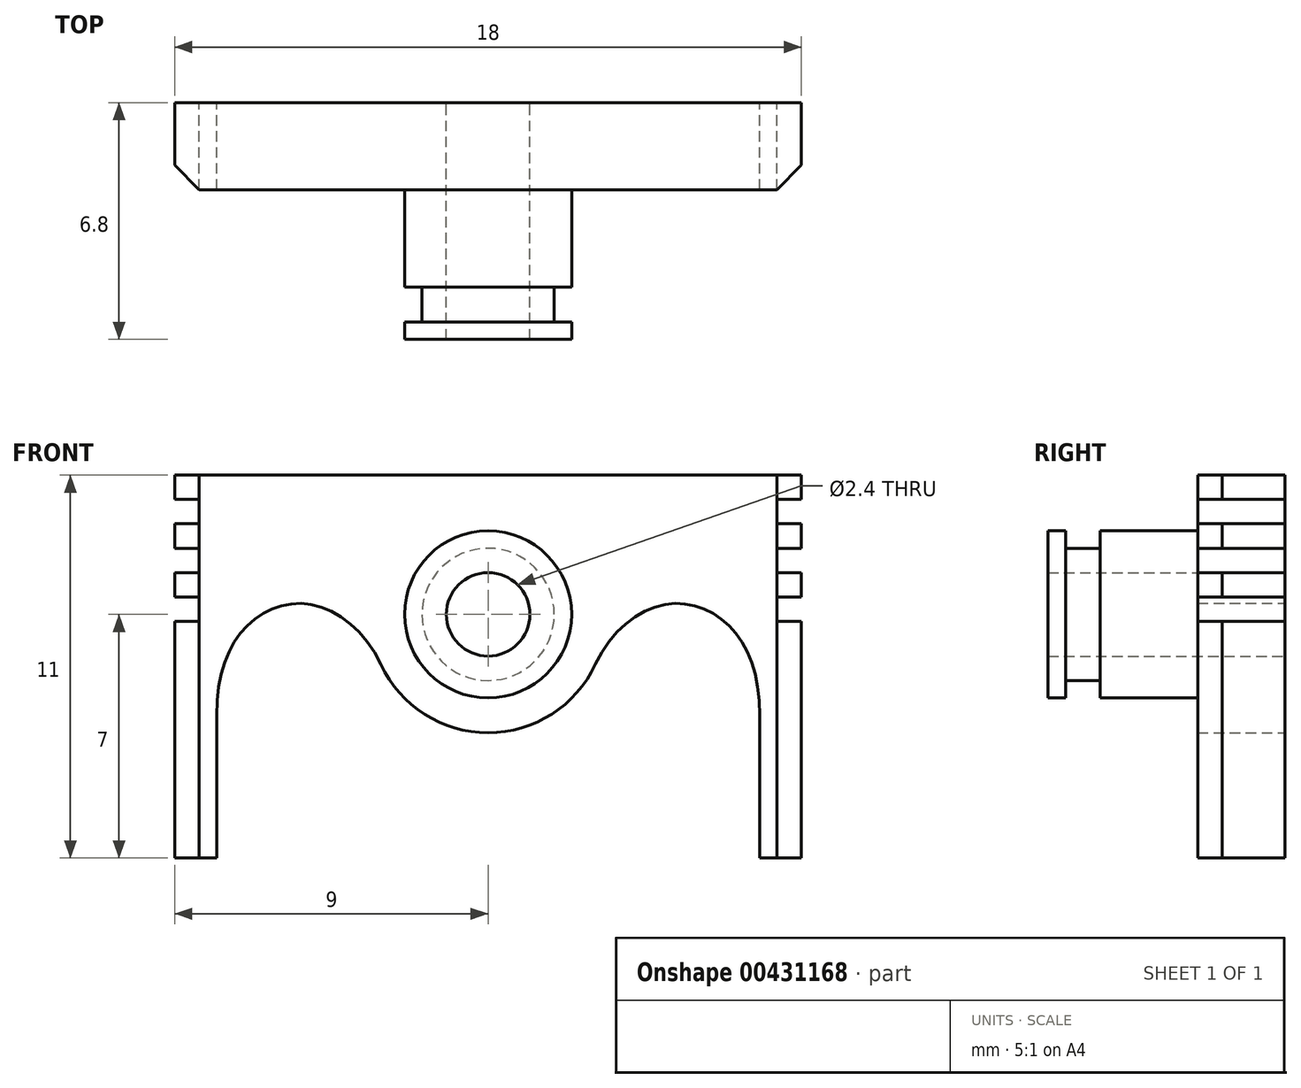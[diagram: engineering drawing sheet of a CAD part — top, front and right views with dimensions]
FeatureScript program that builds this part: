
annotation { "Feature Type Name" : "Feature", "Feature Type Description" : "" }
export const myFeature = defineFeature(function(context is Context, id is Id, definition is map)
    precondition{}
    {
        {
            var Q0;
            Q0=qCreatedBy(makeId("Front.planeOp"),FACE);
            var sketch = newSketch(context, id + "F0", { "sketchPlane" : qUnion([Q0])});
            skLineSegment(sketch, "E0", {"start": v(0, -3.4) * mm, "end": v(0, 25.06) * mm, "construction": true});
            skLineSegment(sketch, "E1.bottom", {"start": v(-9, 4) * mm, "end": v(0, 4) * mm});
            skLineSegment(sketch, "E1.left", {"start": v(-9, 4) * mm, "end": v(-9, 3.3) * mm});
            skArc(sketch, "E2", {"start": v(0, 2.4) * mm, "mid": v(-2.4, 0) * mm, "end": v(0, -2.4) * mm});
            skLineSegment(sketch, "E3.bottom", {"start": v(-9, 3.3) * mm, "end": v(-8.3, 3.3) * mm});
            skLineSegment(sketch, "E3.top", {"start": v(-9, 2.6) * mm, "end": v(-8.3, 2.6) * mm});
            skLineSegment(sketch, "E3.right", {"start": v(-8.3, 3.3) * mm, "end": v(-8.3, 2.6) * mm});
            skLineSegment(sketch, "E4.bottom", {"start": v(-9, 1.9) * mm, "end": v(-8.3, 1.9) * mm});
            skLineSegment(sketch, "E4.top", {"start": v(-9, 1.2) * mm, "end": v(-8.3, 1.2) * mm});
            skLineSegment(sketch, "E4.right", {"start": v(-8.3, 1.9) * mm, "end": v(-8.3, 1.2) * mm});
            skLineSegment(sketch, "E5", {"start": v(-9, 1.9) * mm, "end": v(-9, 2.6) * mm});
            skLineSegment(sketch, "E6", {"start": v(-9, -7) * mm, "end": v(-9, -0.2) * mm});
            skLineSegment(sketch, "E7", {"start": v(-9, -7) * mm, "end": v(-7.8, -7) * mm});
            skLineSegment(sketch, "E8", {"start": v(-7.8, -7) * mm, "end": v(-7.8, -2.9) * mm});
            skLineSegment(sketch, "E9", {"start": v(0, 4) * mm, "end": v(0, 2.4) * mm});
            skLineSegment(sketch, "E10", {"start": v(0, -2.4) * mm, "end": v(0, -3.4) * mm});
            skArc(sketch, "E11", {"start": v(-3.08, -1.44) * mm, "mid": v(-1.83, -2.87) * mm, "end": v(0, -3.4) * mm});
            skFitSpline(sketch, "E12", {"points": [v(-7.8, -2.9) * mm, v(-6.88, -0.29) * mm, v(-5.1, 0.29) * mm, v(-3.08, -1.44) * mm], "startDerivative": vector(0, 10.2) * mm, "endDerivative": vector(3.83, -8.2) * mm});
            skLineSegment(sketch, "E13", {"start": v(-3.08, -1.44) * mm, "end": v(-4.16, 0.88) * mm, "construction": true});
            skLineSegment(sketch, "E14", {"start": v(-9, 0.5) * mm, "end": v(-8.3, 0.5) * mm});
            skLineSegment(sketch, "E15", {"start": v(-8.3, 0.5) * mm, "end": v(-8.3, -0.2) * mm});
            skLineSegment(sketch, "E16", {"start": v(-8.3, -0.2) * mm, "end": v(-9, -0.2) * mm});
            skLineSegment(sketch, "E17.trimOffspring", {"start": v(-9, 0.5) * mm, "end": v(-9, 1.2) * mm});
            skSolve(sketch);
        }
        {
            var Q0;
            Q0=makeQuery(id+"F0.imprint","IMPRINT",FACE,{"disambiguationData":[TD([[makeQuery(id+"F0.imprint","IMPRINT",EDGE,{"derivedFrom":sQuery(id+"F0.wireOp",EDGE,"E1.bottom")}),-1.0]])]});
            extrude(context, id + "F1", {"entities" : qUnion([Q0]), "depth" : 2.5 * mm});
        }
        {
            var Q0;
            Q0=makeQuery(id+"F1.opExtrude","SWEPT_BODY",BODY,{"disambiguationData":[OSD([sQuery(id+"F0.wireOp",EDGE,"E1.bottom"),sQuery(id+"F0.wireOp",EDGE,"E1.left"),sQuery(id+"F0.wireOp",EDGE,"E2"),sQuery(id+"F0.wireOp",EDGE,"E3.bottom"),sQuery(id+"F0.wireOp",EDGE,"E3.top"),sQuery(id+"F0.wireOp",EDGE,"E3.right"),sQuery(id+"F0.wireOp",EDGE,"E4.bottom"),sQuery(id+"F0.wireOp",EDGE,"E4.top"),sQuery(id+"F0.wireOp",EDGE,"E4.right"),sQuery(id+"F0.wireOp",EDGE,"E5"),sQuery(id+"F0.wireOp",EDGE,"E6"),sQuery(id+"F0.wireOp",EDGE,"E7"),sQuery(id+"F0.wireOp",EDGE,"E8"),sQuery(id+"F0.wireOp",EDGE,"E9"),sQuery(id+"F0.wireOp",EDGE,"E10"),sQuery(id+"F0.wireOp",EDGE,"E11"),sQuery(id+"F0.wireOp",EDGE,"E12"),sQuery(id+"F0.wireOp",EDGE,"E14"),sQuery(id+"F0.wireOp",EDGE,"E15"),sQuery(id+"F0.wireOp",EDGE,"E16"),sQuery(id+"F0.wireOp",EDGE,"E17.trimOffspring")])]});
            var Q1;
            Q1=qCreatedBy(makeId("Right.planeOp"),FACE);
            mirror(context, id + "F2", {"operationType" : NewBodyOperationType.ADD, "entities" : qUnion([Q0]), "mirrorPlane" : qUnion([Q1])});
        }
        {
            var Q0;
            Q0=qCreatedBy(makeId("Right.planeOp"),FACE);
            var sketch = newSketch(context, id + "F3", { "sketchPlane" : qUnion([Q0])});
            skLineSegment(sketch, "E18", {"start": v(0, 0) * mm, "end": v(-7.95, 0) * mm, "construction": true});
            skLineSegment(sketch, "E19", {"start": v(-2.5, 2.4) * mm, "end": v(-2.5, 1.2) * mm});
            skLineSegment(sketch, "E20", {"start": v(-2.5, 1.2) * mm, "end": v(-6.8, 1.2) * mm});
            skLineSegment(sketch, "E21", {"start": v(-5.3, 2.4) * mm, "end": v(-2.5, 2.4) * mm});
            skLineSegment(sketch, "E22", {"start": v(-5.3, 2.4) * mm, "end": v(-5.3, 1.9) * mm});
            skLineSegment(sketch, "E23", {"start": v(-5.3, 1.9) * mm, "end": v(-6.3, 1.9) * mm});
            skLineSegment(sketch, "E24", {"start": v(-6.3, 1.9) * mm, "end": v(-6.3, 2.4) * mm});
            skLineSegment(sketch, "E25", {"start": v(-6.3, 2.4) * mm, "end": v(-6.8, 2.4) * mm});
            skLineSegment(sketch, "E26", {"start": v(-6.8, 2.4) * mm, "end": v(-6.8, 1.2) * mm});
            skLineSegment(sketch, "E27", {"start": v(-2.5, 1.2) * mm, "end": v(0, 1.2) * mm});
            skLineSegment(sketch, "E28", {"start": v(0, 1.2) * mm, "end": v(0, 2.4) * mm});
            skLineSegment(sketch, "E29", {"start": v(0, 2.4) * mm, "end": v(-2.5, 2.4) * mm});
            skSolve(sketch);
        }
        {
            var Q0;
            Q0=makeQuery(id+"F1.opExtrude","CAP_EDGE",EDGE,{"disambiguationData":[OSD([sQuery(id+"F0.wireOp",EDGE,"E6")])],"isStart":false});
            var Q1;
            Q1=makeQuery(id+"F2.opPattern","COPY",EDGE,{"derivedFrom":makeQuery(id+"F1.opExtrude","CAP_EDGE",EDGE,{"disambiguationData":[OSD([sQuery(id+"F0.wireOp",EDGE,"E6")])],"isStart":false}),"instanceName":"1"});
            var Q2;
            Q2=makeQuery(id+"F1.opExtrude","CAP_EDGE",EDGE,{"disambiguationData":[OSD([sQuery(id+"F0.wireOp",EDGE,"E1.left")])],"isStart":false});
            var Q3;
            Q3=makeQuery(id+"F1.opExtrude","CAP_EDGE",EDGE,{"disambiguationData":[OSD([sQuery(id+"F0.wireOp",EDGE,"E5")])],"isStart":false});
            var Q4;
            Q4=makeQuery(id+"F1.opExtrude","CAP_EDGE",EDGE,{"disambiguationData":[OSD([sQuery(id+"F0.wireOp",EDGE,"E17.trimOffspring")])],"isStart":false});
            var Q5;
            Q5=makeQuery(id+"F2.opPattern","COPY",EDGE,{"derivedFrom":makeQuery(id+"F1.opExtrude","CAP_EDGE",EDGE,{"disambiguationData":[OSD([sQuery(id+"F0.wireOp",EDGE,"E1.left")])],"isStart":false}),"instanceName":"1"});
            var Q6;
            Q6=makeQuery(id+"F2.opPattern","COPY",EDGE,{"derivedFrom":makeQuery(id+"F1.opExtrude","CAP_EDGE",EDGE,{"disambiguationData":[OSD([sQuery(id+"F0.wireOp",EDGE,"E5")])],"isStart":false}),"instanceName":"1"});
            var Q7;
            Q7=makeQuery(id+"F2.opPattern","COPY",EDGE,{"derivedFrom":makeQuery(id+"F1.opExtrude","CAP_EDGE",EDGE,{"disambiguationData":[OSD([sQuery(id+"F0.wireOp",EDGE,"E17.trimOffspring")])],"isStart":false}),"instanceName":"1"});
            chamfer(context, id + "F4", {"entities" : qUnion([Q0, Q1, Q2, Q3, Q4, Q5, Q6, Q7]), "width" : 0.7 * mm, "tangentPropagation" : true});
        }
        {
            var Q0;
            Q0=makeQuery(id+"F3.imprint","IMPRINT",FACE,{"disambiguationData":[TD([[makeQuery(id+"F3.imprint","IMPRINT",EDGE,{"derivedFrom":sQuery(id+"F3.wireOp",EDGE,"E19")}),-1.0]])]});
            var Q1;
            Q1=makeQuery(id+"F3.imprint","IMPRINT",FACE,{"disambiguationData":[TD([[makeQuery(id+"F3.imprint","IMPRINT",EDGE,{"derivedFrom":sQuery(id+"F3.wireOp",EDGE,"E19")}),1.0]])]});
            var Q2;
            Q2=sQuery(id+"F3.wireOp",EDGE,"E18");
            revolve(context, id + "F5", {"operationType" : NewBodyOperationType.ADD, "entities" : qUnion([Q0, Q1]), "axis" : qUnion([Q2]), "revolveType" : RevolveType.FULL});
        }
    });
